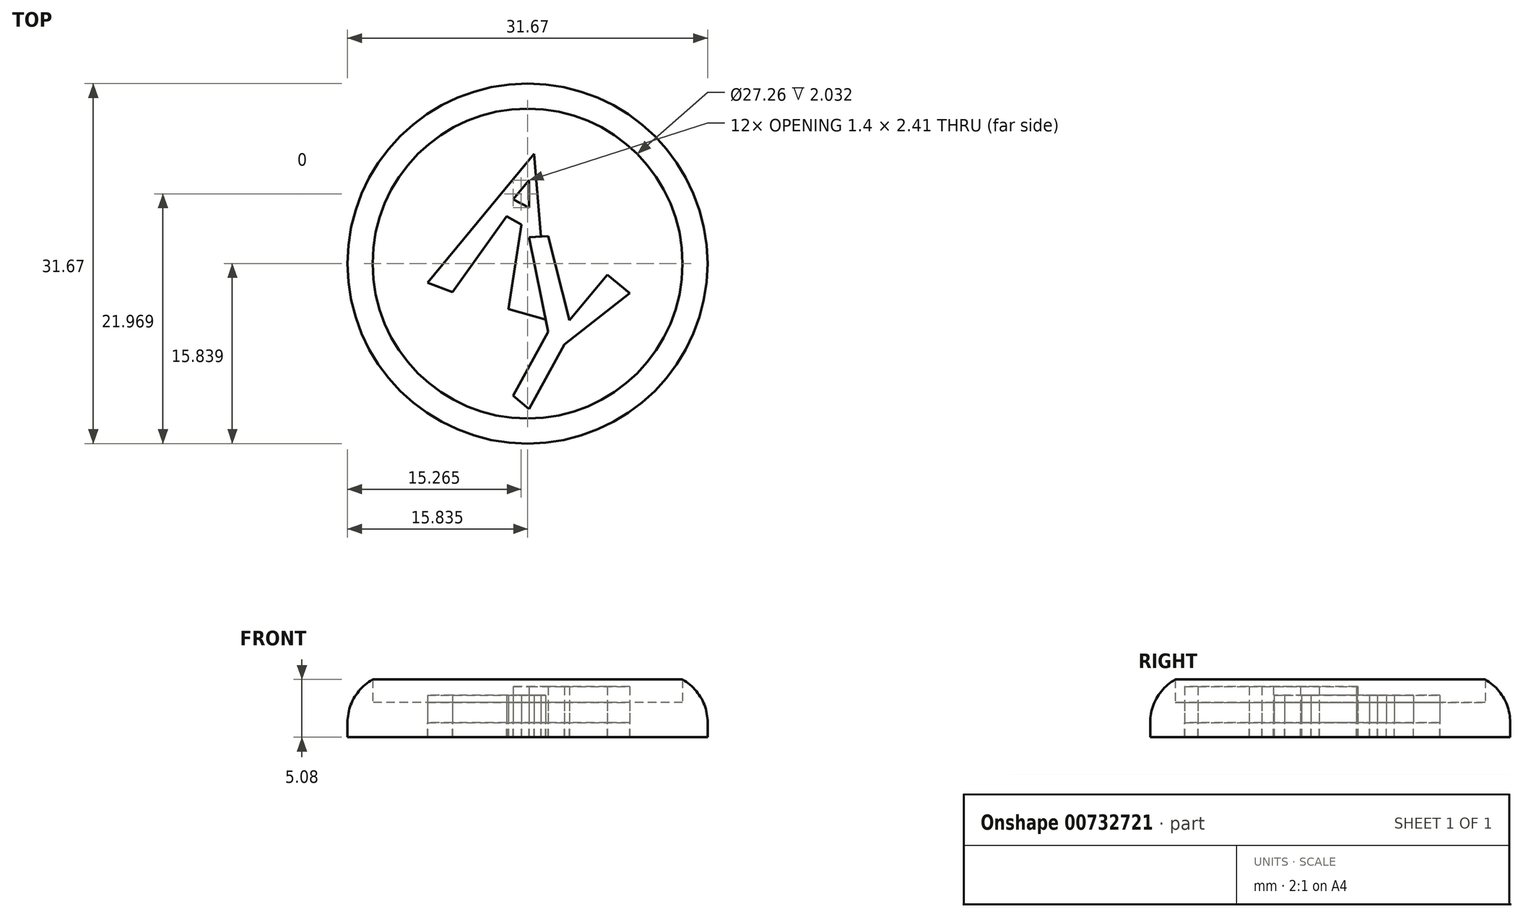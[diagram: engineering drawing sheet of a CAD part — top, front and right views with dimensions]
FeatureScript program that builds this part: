
annotation { "Feature Type Name" : "Feature", "Feature Type Description" : "" }
export const myFeature = defineFeature(function(context is Context, id is Id, definition is map)
    precondition{}
    {
        {
            var Q0;
            Q0=qCreatedBy(makeId("Top.planeOp"),FACE);
            var sketch = newSketch(context, id + "F0", { "sketchPlane" : qUnion([Q0])});
            skLineSegment(sketch, "E0", {"start": v(-125.94, 24.67) * mm, "end": v(-116.56, 35.98) * mm});
            skLineSegment(sketch, "E1", {"start": v(-116.56, 35.98) * mm, "end": v(-115.32, 21.35) * mm});
            skLineSegment(sketch, "E2", {"start": v(-115.32, 21.35) * mm, "end": v(-118.83, 22.34) * mm});
            skLineSegment(sketch, "E3", {"start": v(-118.83, 22.34) * mm, "end": v(-117.67, 29.79) * mm});
            skLineSegment(sketch, "E4", {"start": v(-117.67, 29.79) * mm, "end": v(-118.98, 30.5) * mm});
            skLineSegment(sketch, "E5", {"start": v(-118.98, 30.5) * mm, "end": v(-123.73, 23.83) * mm});
            skLineSegment(sketch, "E6", {"start": v(-123.73, 23.83) * mm, "end": v(-125.94, 24.67) * mm});
            skLineSegment(sketch, "E7", {"start": v(-118.4, 32) * mm, "end": v(-117, 33.68) * mm});
            skLineSegment(sketch, "E8", {"start": v(-117, 33.68) * mm, "end": v(-117, 31.28) * mm});
            skLineSegment(sketch, "E9", {"start": v(-117, 31.28) * mm, "end": v(-118.4, 32) * mm});
            skLineSegment(sketch, "E10", {"start": v(-117, 28.67) * mm, "end": v(-115.32, 20.35) * mm});
            skPoint(sketch, "E10.startSnap0", {"position": v(-115.94, 28.67) * mm});
            skLineSegment(sketch, "E11", {"start": v(-115.32, 20.35) * mm, "end": v(-118.4, 14.72) * mm});
            skLineSegment(sketch, "E12", {"start": v(-118.4, 14.72) * mm, "end": v(-117, 13.56) * mm});
            skLineSegment(sketch, "E13", {"start": v(-117, 13.56) * mm, "end": v(-113.9, 19.22) * mm});
            skLineSegment(sketch, "E14", {"start": v(-113.9, 19.22) * mm, "end": v(-108.14, 23.75) * mm});
            skLineSegment(sketch, "E15", {"start": v(-108.14, 23.75) * mm, "end": v(-110.1, 25.38) * mm});
            skLineSegment(sketch, "E16", {"start": v(-110.1, 25.38) * mm, "end": v(-113.45, 21.35) * mm});
            skLineSegment(sketch, "E17", {"start": v(-113.45, 21.35) * mm, "end": v(-115.32, 28.77) * mm});
            skLineSegment(sketch, "E18", {"start": v(-115.32, 28.77) * mm, "end": v(-117, 28.67) * mm});
            skCircle(sketch, "E19", {"center": v(-117.14, 26.35) * mm, "radius": 13.63 * mm});
            skCircle(sketch, "E20", {"center": v(-117.14, 26.35) * mm, "radius": 15.83 * mm});
            skSolve(sketch);
        }
        {
            var Q0;
            {var subQ4=sQuery(id+"F0.wireOp",EDGE,"E0");Q0=makeQuery(id+"F0.imprint","IMPRINT",FACE,{"disambiguationData":[TD([[makeQuery(id+"F0.imprint","IMPRINT",EDGE,{"derivedFrom":subQ4}),1.0]])]});}
            var Q1;
            Q1=makeQuery(id+"F0.imprint","IMPRINT",FACE,{"disambiguationData":[TD([[makeQuery(id+"F0.imprint","IMPRINT",EDGE,{"derivedFrom":sQuery(id+"F0.wireOp",EDGE,"E7")}),-1.0]])]});
            extrude(context, id + "F1", {"entities" : qUnion([Q0, Q1]), "depth" : 1.78 * mm, "offsetDistance" : 25.4 * mm});
        }
        {
            var Q0;
            Q0 = qSketchRegion(id + "F0", true);
            extrude(context, id + "F2", {"entities" : qUnion([Q0]), "operationType" : NewBodyOperationType.ADD, "depth" : 3.8 * mm, "offsetDistance" : 25.4 * mm});
        }
        {
            var Q0;
            {var subQ0=sQuery(id+"F0.wireOp",EDGE,"E0");Q0=makeQuery(id+"F0.imprint","IMPRINT",FACE,{"disambiguationData":[TD([[makeQuery(id+"F0.imprint","IMPRINT",EDGE,{"derivedFrom":subQ0}),-1.0]])]});}
            extrude(context, id + "F3", {"entities" : qUnion([Q0]), "depth" : 2.41 * mm, "offsetDistance" : 25.4 * mm});
        }
        {
            var Q0;
            {var subQ0=sQuery(id+"F0.wireOp",EDGE,"E2");var subQ1=sQuery(id+"F0.wireOp",EDGE,"E1");var subQ2=makeQuery(id+"F0.imprint","INTERSECT",VERTEX,{"derivedFrom":[subQ1,subQ0]});Q0=makeQuery(id+"F0.imprint","IMPRINT",FACE,{"disambiguationData":[TD([[makeQuery(id+"F0.imprint","IMPRINT",EDGE,{"disambiguationData":[TD([[subQ2,1.0]])],"derivedFrom":subQ1}),-1.0]])]});}
            var Q1;
            {var subQ6=sQuery(id+"F0.wireOp",EDGE,"E11");Q1=makeQuery(id+"F0.imprint","IMPRINT",FACE,{"disambiguationData":[TD([[makeQuery(id+"F0.imprint","IMPRINT",EDGE,{"derivedFrom":subQ6}),1.0]])]});}
            extrude(context, id + "F4", {"entities" : qUnion([Q0, Q1]), "depth" : 3.17 * mm, "offsetDistance" : 25.4 * mm});
        }
        {
            var Q0;
            {var subQ0=sQuery(id+"F0.wireOp",EDGE,"E19");Q0=makeQuery(id+"F2.boolean.opBoolean","MERGE",FACE,{"derivedFrom":[makeQuery(id+"F1.opExtrude","CAP_FACE",FACE,{"disambiguationData":[OSD([sQuery(id+"F0.wireOp",EDGE,"E0"),sQuery(id+"F0.wireOp",EDGE,"E1"),sQuery(id+"F0.wireOp",EDGE,"E2"),sQuery(id+"F0.wireOp",EDGE,"E3"),sQuery(id+"F0.wireOp",EDGE,"E4"),sQuery(id+"F0.wireOp",EDGE,"E5"),sQuery(id+"F0.wireOp",EDGE,"E6"),sQuery(id+"F0.wireOp",EDGE,"E10"),sQuery(id+"F0.wireOp",EDGE,"E11"),sQuery(id+"F0.wireOp",EDGE,"E12"),sQuery(id+"F0.wireOp",EDGE,"E13"),sQuery(id+"F0.wireOp",EDGE,"E14"),sQuery(id+"F0.wireOp",EDGE,"E15"),sQuery(id+"F0.wireOp",EDGE,"E16"),sQuery(id+"F0.wireOp",EDGE,"E17"),sQuery(id+"F0.wireOp",EDGE,"E18"),subQ0])],"isStart":true}),makeQuery(id+"F2.opExtrude","CAP_FACE",FACE,{"disambiguationData":[OSD([subQ0,sQuery(id+"F0.wireOp",EDGE,"E20")])],"isStart":true})]});}
            var Q1;
            Q1=makeQuery(id+"F4.opExtrude","CAP_FACE",FACE,{"disambiguationData":[OSD([sQuery(id+"F0.wireOp",EDGE,"E10"),sQuery(id+"F0.wireOp",EDGE,"E11"),sQuery(id+"F0.wireOp",EDGE,"E12"),sQuery(id+"F0.wireOp",EDGE,"E13"),sQuery(id+"F0.wireOp",EDGE,"E14"),sQuery(id+"F0.wireOp",EDGE,"E15"),sQuery(id+"F0.wireOp",EDGE,"E16"),sQuery(id+"F0.wireOp",EDGE,"E17"),sQuery(id+"F0.wireOp",EDGE,"E18")])],"isStart":true});
            var Q2;
            Q2=makeQuery(id+"F3.opExtrude","CAP_FACE",FACE,{"disambiguationData":[OSD([sQuery(id+"F0.wireOp",EDGE,"E0"),sQuery(id+"F0.wireOp",EDGE,"E1"),sQuery(id+"F0.wireOp",EDGE,"E2"),sQuery(id+"F0.wireOp",EDGE,"E3"),sQuery(id+"F0.wireOp",EDGE,"E4"),sQuery(id+"F0.wireOp",EDGE,"E5"),sQuery(id+"F0.wireOp",EDGE,"E6"),sQuery(id+"F0.wireOp",EDGE,"E7"),sQuery(id+"F0.wireOp",EDGE,"E8"),sQuery(id+"F0.wireOp",EDGE,"E9"),sQuery(id+"F0.wireOp",EDGE,"E10"),sQuery(id+"F0.wireOp",EDGE,"E18")])],"isStart":true});
            var Q3;
            Q3=makeQuery(id+"F1.opExtrude","CAP_FACE",FACE,{"disambiguationData":[OSD([sQuery(id+"F0.wireOp",EDGE,"E7"),sQuery(id+"F0.wireOp",EDGE,"E8"),sQuery(id+"F0.wireOp",EDGE,"E9")])],"isStart":true});
            extrude(context, id + "F5", {"entities" : qUnion([Q0, Q1, Q2, Q3]), "depth" : 1.27 * mm, "offsetDistance" : 25.4 * mm});
        }
        {
            var Q0;
            Q0=makeQuery(id+"F2.opExtrude","CAP_EDGE",EDGE,{"disambiguationData":[OSD([sQuery(id+"F0.wireOp",EDGE,"E20")])],"isStart":false});
            fillet(context, id + "F6", {"entities" : qUnion([Q0]), "radius" : 4.35 * mm, "tangentPropagation" : true, "allowEdgeOverflow" : false});
        }
    });
